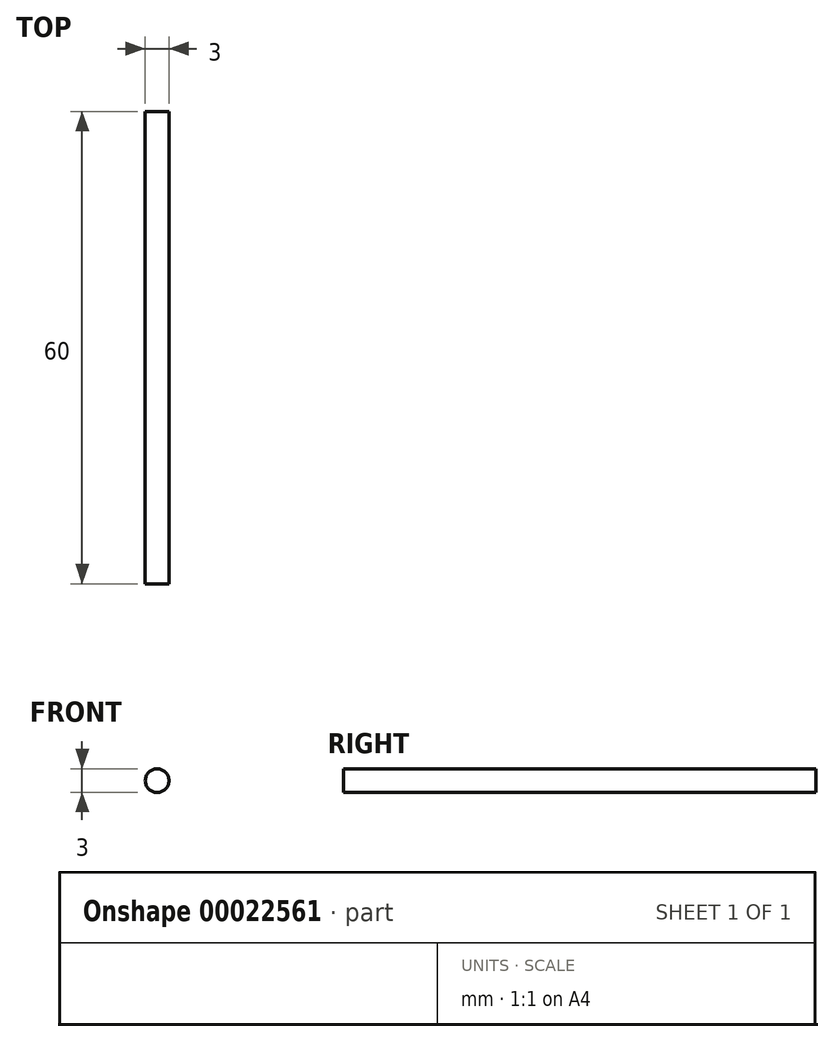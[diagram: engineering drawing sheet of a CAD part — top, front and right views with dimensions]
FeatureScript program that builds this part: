
annotation { "Feature Type Name" : "Feature", "Feature Type Description" : "" }
export const myFeature = defineFeature(function(context is Context, id is Id, definition is map)
    precondition{}
    {
        {
            var Q0;
            Q0=qCreatedBy(makeId("Front.planeOp"),FACE);
            var sketch = newSketch(context, id + "F0", { "sketchPlane" : qUnion([Q0])});
            skCircle(sketch, "E0", {"center": v(-19.98, 7.14) * mm, "radius": 1.5 * mm});
            skSolve(sketch);
        }
        {
            var Q0;
            Q0=makeQuery(id+"F0.imprint","IMPRINT",FACE,{"disambiguationData":[TD([[makeQuery(id+"F0.imprint","IMPRINT",EDGE,{"derivedFrom":sQuery(id+"F0.wireOp",EDGE,"E0")}),1.0]])]});
            extrude(context, id + "F1", {"entities" : qUnion([Q0]), "depth" : 60 * mm});
        }
    });
